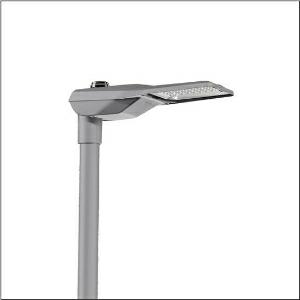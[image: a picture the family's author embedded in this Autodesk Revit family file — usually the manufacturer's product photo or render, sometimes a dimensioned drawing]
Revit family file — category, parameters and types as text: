
# Revit family: streetlight_sl_21_mini___p0_8a_5xe6u47n08gb_070e
name_source: partatom
category: Lighting Fixtures
units: mm (PartAtom-declared; Revit-internal decimal feet)

## family parameters
Cut with Voids When Loaded = No
Host = Face
Light Source = No
Part Type = Normal
Room Calculation Point = No
Round Connector Dimension = Use Diameter
Shared = No

## types (1)
- --- (1 x LED, 6240 lm, 40.4 W, 4000K)
    Apparent Load = 40 VA
    CIE Flux Codes = 33 69 96 100 100
    Color Rendering = 70
    Color Temperature = 4000K
    Default Elevation = 1800 mm
    Description = Streetlight SL 21 mini, mast luminaire, primary light control with lens, of PMMA, primary optical cover: cover, of toughened safety glass, transparent, light distribution: P0.8a, light emission: direct distribution, primary light characteristic: asymmetric, installation type: side-entry, LED, 3G 1.5mm², High Power LED, rated luminous flux: 6.240lm, luminous efficacy: 155lm/W, light colour: 740, colour temperature: 4000K, control gear: NEMA (7pin), control: flexible luminous flux parameterisation, time-dependent luminous flux control, constant luminous flux control, pre-setting: linear dimming characteristic, overheat protection, mains connection: 230..240V, AC, 50/60Hz, connection cable pre-assembled, cable length: 8,5m, wiring characteristics: H07RN-F, start of lifetime: 40W, end of service life: 41W, reduction: 19W, luminaire housing, of diecast aluminium (EN AC-44300), powder-coated, Siteco® metallic grey (DB 702S), corrosivity category C5 mid according to DIN EN ISO 12944, multi-level sealing system, sealing non-destructively replaceable, inclination adjustable: 0°, 5°, 10°, 15°, length: 628mm, width: 235mm, height: 110mm, spigot size: 42mm (side-entry), mounting height: 4..8m, protection rating (complete): IP66, insulation class (complete): insulation class I (protective earthing), certification: CE, ENEC, ENEC+, VDE, impact resistance: IK10, permissible operating ambient temperature for outdoor applications: -40..+50°C, standard-compliant lighting for roads and squares, packaging unit: 1 piece

Light Distribution: P0.8a
    Height = 110 mm
    Lamp = 1 x LED
    Lamp Light Flux = 6240 lm
    Lamp Power = 40.4 W
    Lamp count = 1
    Length = 625 mm
    Luminous efficacy = 154 lm/W
    Manufacturer = Siteco
    ModVariant = No
    Model = 5XE6U47N08GB
    Number of Poles = 1
    OnlyDefault = Yes
    Power Factor = 1
    Product Name = Streetlight SL 21 mini | P0.8a
    Product group = mast luminaire | pylon top
    ProductGroupID = 6100
    Protection Class = Protection class I
    Protection Degree = IP 66
    RLX_Detail_Level = 1
    RLX_Emergency_Light_Flux = 0 lm
    RLX_Emergency_Type = 0
    RLX_Emergency_Type_DB = No
    RlxData = <blob elided: 25633 chars, md5=bf0c0509>
    Socket = socket
    Standby Power = 0 W
    System Light Flux = 6240 lm
    System Power = 40 W
    Type Comments = factory setting: luminous flux: 100 % | dim-lin: 254 | 812 mA
    Type Image = l_1294379.jpg
    URL = http://relux.com
    VarID = @adj_073544
    Voltage = 0 V
    Weight = 0.00 kg
    Width = 234 mm

## geometry (parser evidence)
native form markers: Blend x4, Sweep x10
no freeform markers — native parametric forms only
